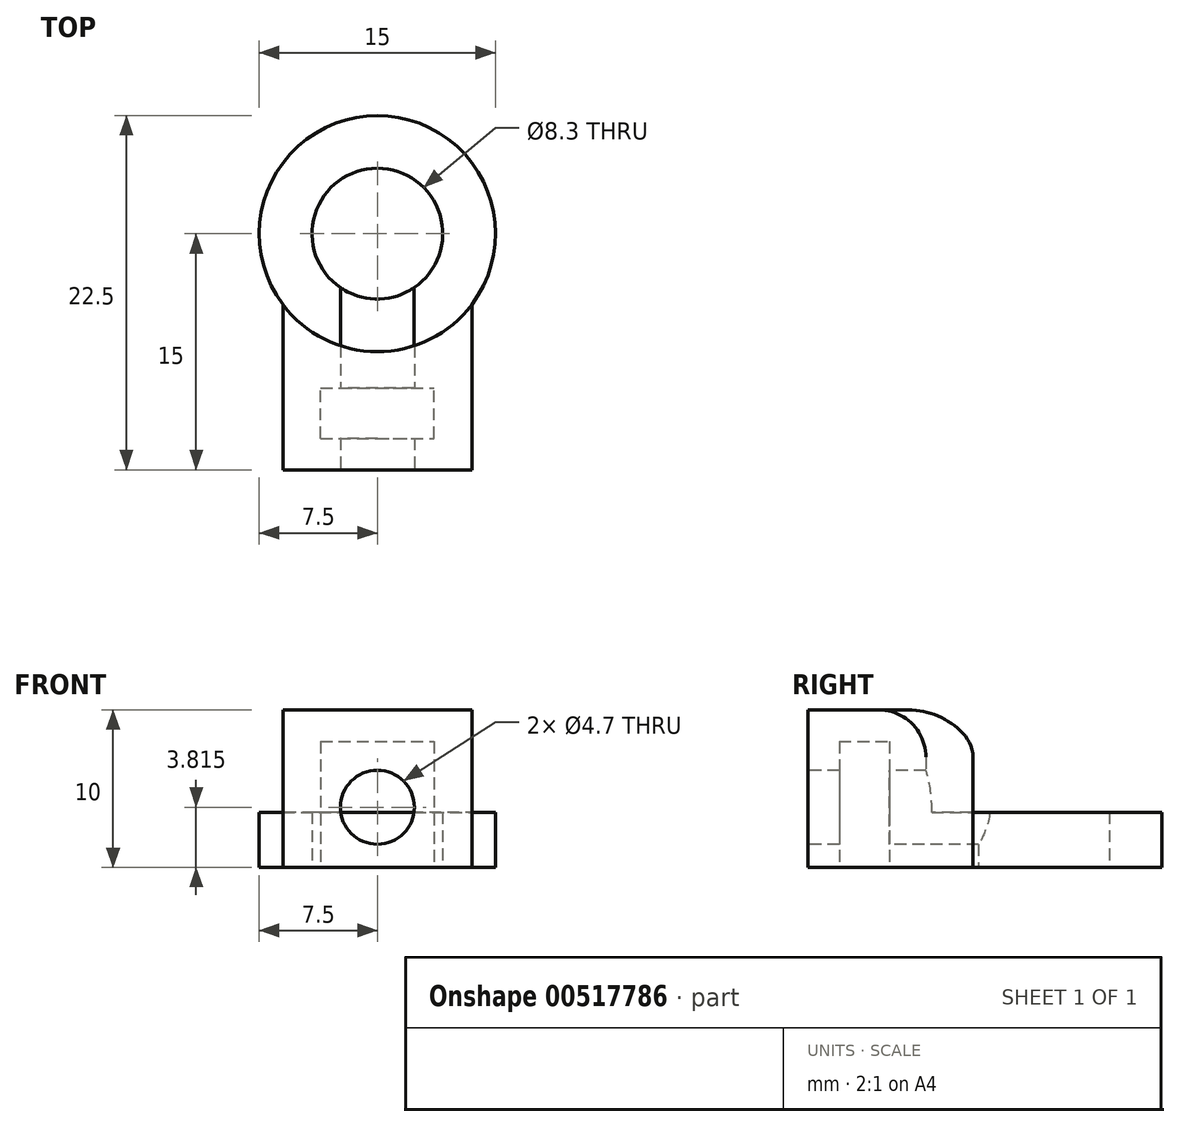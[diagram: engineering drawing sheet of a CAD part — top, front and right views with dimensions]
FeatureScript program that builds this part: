
annotation { "Feature Type Name" : "Feature", "Feature Type Description" : "" }
export const myFeature = defineFeature(function(context is Context, id is Id, definition is map)
    precondition{}
    {
        {
            var Q0;
            Q0=qCreatedBy(makeId("Top.planeOp"),FACE);
            var sketch = newSketch(context, id + "F0", { "sketchPlane" : qUnion([Q0])});
            skCircle(sketch, "E0", {"center": v(0, 0) * mm, "radius": 7.5 * mm});
            skLineSegment(sketch, "E1.top", {"start": v(-6, -15) * mm, "end": v(6, -15) * mm});
            skLineSegment(sketch, "E1.left", {"start": v(-6, -4.5) * mm, "end": v(-6, -15) * mm});
            skLineSegment(sketch, "E1.right", {"start": v(6, -4.5) * mm, "end": v(6, -15) * mm});
            skCircle(sketch, "E2", {"center": v(0, 0) * mm, "radius": 4.15 * mm});
            skSolve(sketch);
        }
        {
            var Q0;
            Q0=makeQuery(id+"F0.imprint","IMPRINT",FACE,{"disambiguationData":[TD([[makeQuery(id+"F0.imprint","IMPRINT",EDGE,{"derivedFrom":sQuery(id+"F0.wireOp",EDGE,"E2")}),-1.0]])]});
            extrude(context, id + "F1", {"entities" : qUnion([Q0]), "depth" : 3.5 * mm, "offsetDistance" : 25 * mm});
        }
        {
            var Q0;
            Q0=makeQuery(id+"F0.imprint","IMPRINT",FACE,{"disambiguationData":[TD([[makeQuery(id+"F0.imprint","IMPRINT",EDGE,{"derivedFrom":sQuery(id+"F0.wireOp",EDGE,"E1.top")}),1.0]])]});
            extrude(context, id + "F2", {"entities" : qUnion([Q0]), "operationType" : NewBodyOperationType.ADD, "depth" : 10 * mm, "offsetDistance" : 25 * mm});
        }
        {
            var Q0;
            Q0=makeQuery(id+"F2.opExtrude","SWEPT_FACE",FACE,{"disambiguationData":[OSD([sQuery(id+"F0.wireOp",EDGE,"E1.top")])]});
            var sketch = newSketch(context, id + "F3", { "sketchPlane" : qUnion([Q0])});
            skCircle(sketch, "E3", {"center": v(0, 3.81) * mm, "radius": 3.81 * mm, "construction": true});
            skCircle(sketch, "E4", {"center": v(0, 3.81) * mm, "radius": 2.35 * mm});
            skSolve(sketch);
        }
        {
            var Q0;
            Q0 = qSketchRegion(id + "F3", true);
            var Q1;
            Q1=makeQuery(id+"F1.opExtrude","SWEPT_FACE",FACE,{"disambiguationData":[OSD([sQuery(id+"F0.wireOp",EDGE,"E2")])]});
            extrude(context, id + "F4", {"entities" : qUnion([Q0]), "operationType" : NewBodyOperationType.REMOVE, "endBound" : BoundingType.UP_TO_SURFACE, "oppositeDirection" : true, "depth" : 15 * mm, "endBoundEntityFace" : qUnion([Q1]), "offsetDistance" : 25 * mm});
        }
        {
            var Q0;
            Q0=makeQuery(id+"F0.imprint","IMPRINT",FACE,{"disambiguationData":[TD([[makeQuery(id+"F0.imprint","IMPRINT",EDGE,{"derivedFrom":sQuery(id+"F0.wireOp",EDGE,"E1.top")}),1.0]])]});
            var sketch = newSketch(context, id + "F5", { "sketchPlane" : qUnion([Q0])});
            skLineSegment(sketch, "E5.bottom", {"start": v(-3.6, -13) * mm, "end": v(3.6, -13) * mm});
            skLineSegment(sketch, "E5.top", {"start": v(-3.6, -9.8) * mm, "end": v(3.6, -9.8) * mm});
            skLineSegment(sketch, "E5.left", {"start": v(-3.6, -13) * mm, "end": v(-3.6, -9.8) * mm});
            skLineSegment(sketch, "E5.right", {"start": v(3.6, -13) * mm, "end": v(3.6, -9.8) * mm});
            skPoint(sketch, "E6", {"position": v(0, -13) * mm});
            skSolve(sketch);
        }
        {
            var Q0;
            Q0 = qSketchRegion(id + "F5", true);
            extrude(context, id + "F6", {"entities" : qUnion([Q0]), "operationType" : NewBodyOperationType.REMOVE, "depth" : 8 * mm, "offsetDistance" : 25 * mm});
        }
        {
            var Q0;
            Q0=makeQuery(id+"F2.opExtrude","CAP_EDGE",EDGE,{"disambiguationData":[OSD([sQuery(id+"F0.wireOp",EDGE,"E0")])],"isStart":false});
            fillet(context, id + "F7", {"entities" : qUnion([Q0]), "radius" : 3 * mm, "tangentPropagation" : true, "allowEdgeOverflow" : false});
        }
    });
